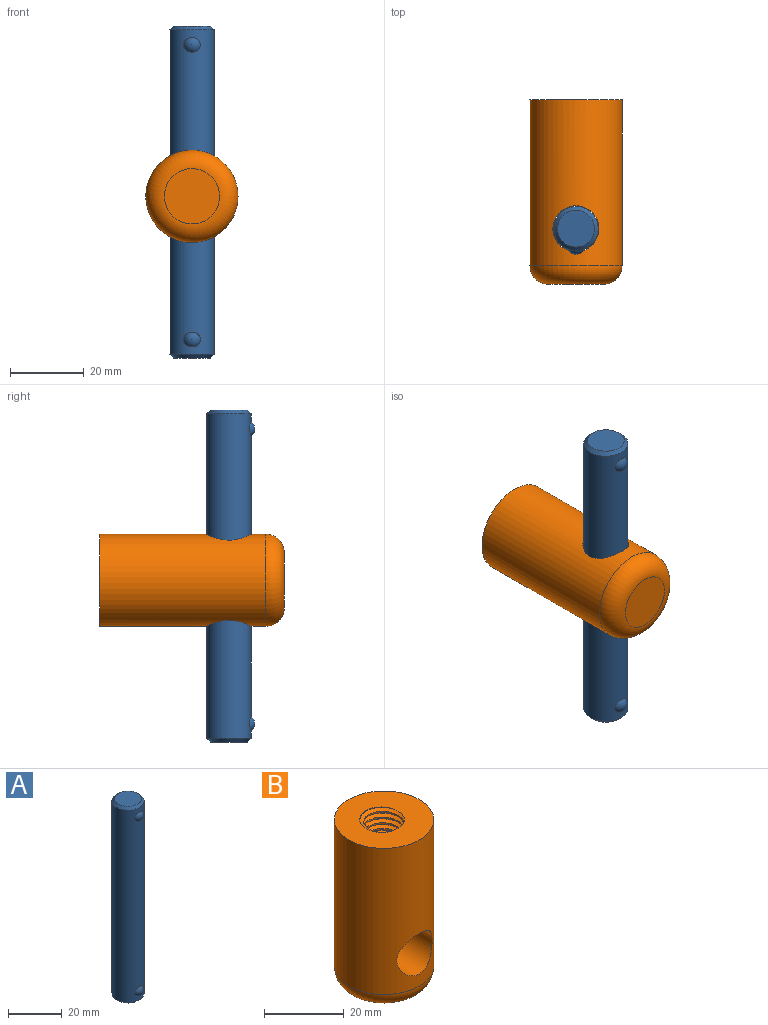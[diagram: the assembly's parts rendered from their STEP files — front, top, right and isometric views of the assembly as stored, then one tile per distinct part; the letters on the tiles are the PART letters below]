
ASSEMBLY  parts=2 mates=1
PART A: 7 faces, bbox 12x13x90 mm
  f0: cylinder r=6mm len=88mm, axis (0,0,-1), area 3288.4mm2, adj f3,f4,f5,f6
  f1: plane 10x10mm, normal (0,0,1), area 78.5mm2, adj f3
  f2: plane 10x10mm, normal (0,0,-1), area 78.5mm2, adj f4
  f3: cone r=5mm half-angle=45deg, axis (0,0,-1), area 48.9mm2, adj f0,f1
  f4: cone r=6mm half-angle=45deg, axis (0,0,1), area 48.9mm2, adj f0,f2
  f5: sphere r=2.5mm, area 19mm2, adj f0
  f6: sphere r=2.5mm, area 19mm2, adj f0
PART B: 12 faces, bbox 27.6x27.6x51.2 mm
  f0: cylinder r=12.5mm len=45mm, axis (0,0,-1), area 3280.2mm2, adj f1,f10,f11
  f1: plane 25.52x25.52mm, normal (0,0,1), area 393.9mm2, adj f0,f4,f5,f6,f9
  f2: plane 15x15mm, normal (0,0,-1), area 176.7mm2, adj f11
  f3: cone r=0mm half-angle=59deg, axis (0,0,1), area 131.9mm2, adj f7,f8
  f4: bspline ~26.21x14.02mm, area 549.6mm2, adj f1,f6,f7,f8,f9
  f5: bspline ~26.51x14.02mm, area 550.6mm2, adj f1,f6,f7,f8,f9
  f6: bspline ~25.59x14.21mm, area 138.4mm2, adj f1,f4,f5,f7
  f7: plane 5.29x3.38mm, normal (0,0,1), area 0.6mm2, adj f3,f4,f5,f6
  f8: plane 12.43x12.43mm, normal (0,0,-1), area 16.7mm2, adj f3,f4,f5,f9
  f9: cylinder r=5.12mm len=25mm, axis (0,0,-1), area 225mm2, adj f1,f4,f5,f8
  f10: cylinder r=6.25mm len=25mm, axis (0,-1,0), area 917.2mm2, adj f0
  f11: torus R=7.5mm, axis (0,0,1), area 527.2mm2, adj f0,f2
PLACE A t=(-30.58,-14.77,-22.48)mm
PLACE B rot(axis=(-1,0,0),90deg) t=(-30.58,-29.77,21.35)mm
MATE pin_slot B.f10 <-> A.f0  axis (0,0,1) through (-30.58,-14.77,34.02)mm
